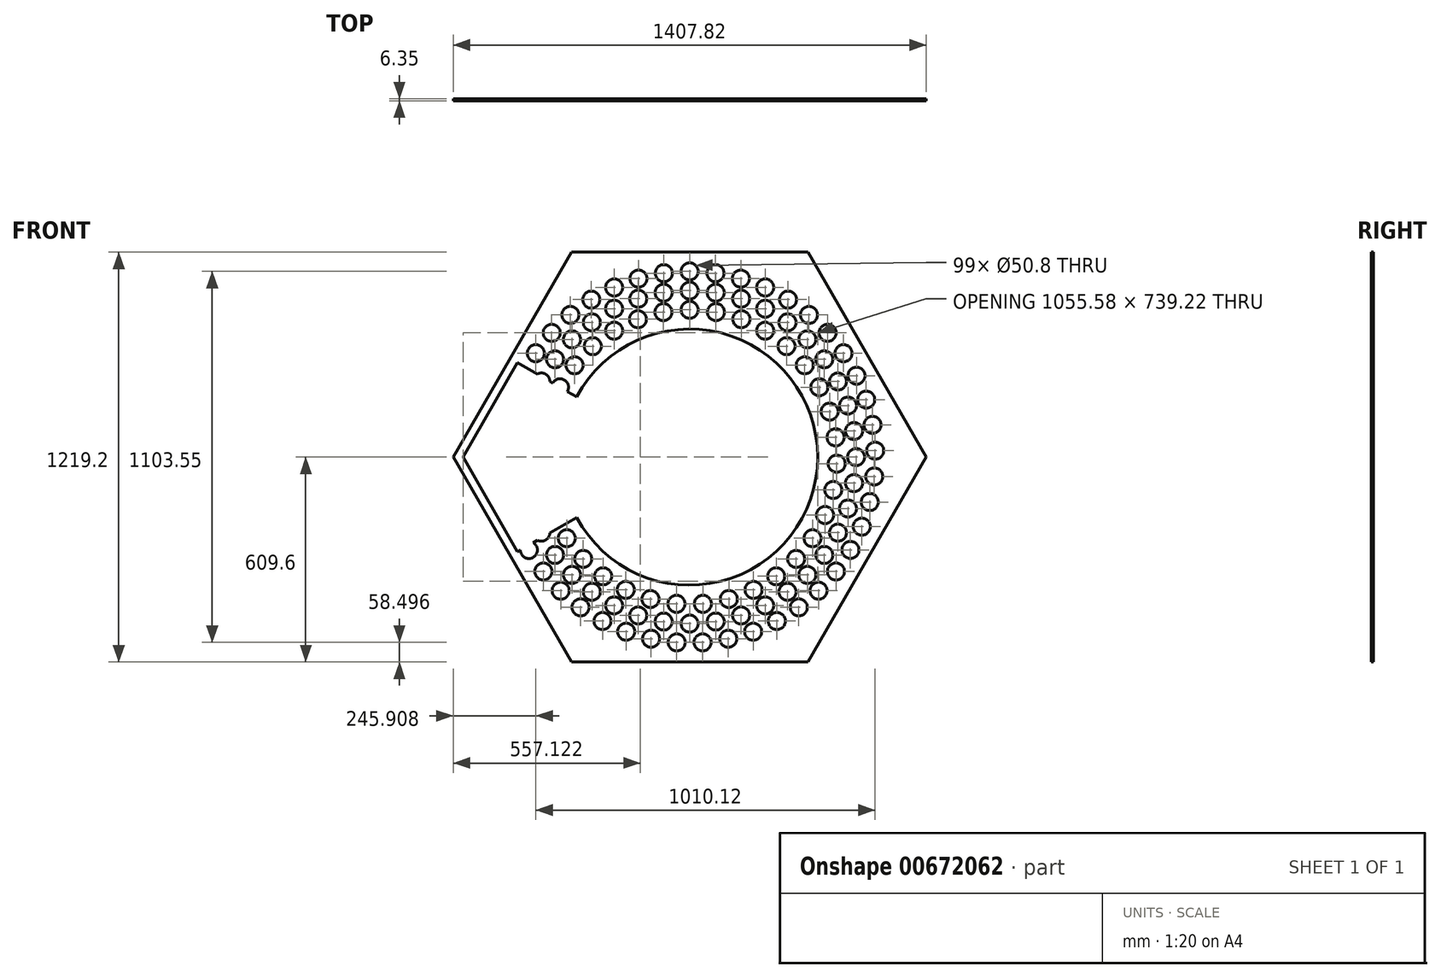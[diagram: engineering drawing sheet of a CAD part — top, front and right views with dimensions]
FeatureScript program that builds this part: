
annotation { "Feature Type Name" : "Feature", "Feature Type Description" : "" }
export const myFeature = defineFeature(function(context is Context, id is Id, definition is map)
    precondition{}
    {
        {
            var Q0;
            Q0=qCreatedBy(makeId("Front.planeOp"),FACE);
            var sketch = newSketch(context, id + "F0", { "sketchPlane" : qUnion([Q0])});
            skCircle(sketch, "E0.cCircle", {"center": v(0, 0) * mm, "radius": 584.2 * mm, "construction": true});
            skLineSegment(sketch, "E0.0", {"start": v(337.29, 584.2) * mm, "end": v(674.58, 0) * mm});
            skLineSegment(sketch, "E0.1", {"start": v(674.58, 0) * mm, "end": v(337.29, -584.2) * mm});
            skLineSegment(sketch, "E0.2", {"start": v(337.29, -584.2) * mm, "end": v(-337.29, -584.2) * mm});
            skLineSegment(sketch, "E0.3", {"start": v(-337.29, -584.2) * mm, "end": v(-674.58, 0) * mm});
            skLineSegment(sketch, "E0.4", {"start": v(-674.58, 0) * mm, "end": v(-499.58, 303.1) * mm});
            skLineSegment(sketch, "E0.5", {"start": v(-337.29, 584.2) * mm, "end": v(337.29, 584.2) * mm});
            skPoint(sketch, "E0.0.midPoint", {"position": v(505.93, 292.1) * mm});
            skCircle(sketch, "E1", {"center": v(0, 0) * mm, "radius": 381 * mm});
            skLineSegment(sketch, "E2", {"start": v(-512.28, 281.1) * mm, "end": v(-336.12, 179.4) * mm});
            skLineSegment(sketch, "E3", {"start": v(-499.58, 303.1) * mm, "end": v(-323.42, 201.4) * mm});
            skLineSegment(sketch, "E4", {"start": v(-337.29, 584.2) * mm, "end": v(-337.29, 584.2) * mm});
            skLineSegment(sketch, "E5", {"start": v(-512.28, 281.1) * mm, "end": v(-337.29, 584.2) * mm});
            skLineSegment(sketch, "E6", {"start": v(-499.58, 303.1) * mm, "end": v(-466.29, 360.76) * mm});
            skLineSegment(sketch, "E7", {"start": v(-674.58, 0) * mm, "end": v(-674.58, 0) * mm});
            skLineSegment(sketch, "E8", {"start": v(-1099.5, 381) * mm, "end": v(1284.02, 381) * mm, "construction": true});
            skLineSegment(sketch, "E9", {"start": v(-1101.82, -381) * mm, "end": v(1466.6, -381) * mm, "construction": true});
            skLineSegment(sketch, "E10.1.0", {"start": v(-499.58, -303.1) * mm, "end": v(-323.42, -201.4) * mm});
            skLineSegment(sketch, "E10.1.1", {"start": v(-512.28, -281.1) * mm, "end": v(-336.12, -179.4) * mm});
            skLineSegment(sketch, "E10.2.0", {"start": v(12.7, -584.2) * mm, "end": v(12.7, -380.79) * mm});
            skLineSegment(sketch, "E10.2.1", {"start": v(-12.7, -584.2) * mm, "end": v(-12.7, -380.79) * mm});
            skLineSegment(sketch, "E10.3.0", {"start": v(512.28, -281.1) * mm, "end": v(336.12, -179.4) * mm});
            skLineSegment(sketch, "E10.3.1", {"start": v(499.58, -303.1) * mm, "end": v(323.42, -201.4) * mm});
            skLineSegment(sketch, "E10.4.0", {"start": v(499.58, 303.1) * mm, "end": v(323.42, 201.4) * mm});
            skLineSegment(sketch, "E10.4.1", {"start": v(512.28, 281.1) * mm, "end": v(336.12, 179.4) * mm});
            skLineSegment(sketch, "E10.5.0", {"start": v(-12.7, 584.2) * mm, "end": v(-12.7, 380.79) * mm});
            skLineSegment(sketch, "E10.5.1", {"start": v(12.7, 584.2) * mm, "end": v(12.7, 380.79) * mm});
            skCircle(sketch, "E11.cCircle", {"center": v(0, 0) * mm, "radius": 609.6 * mm, "construction": true});
            skLineSegment(sketch, "E11.0", {"start": v(-351.95, 609.6) * mm, "end": v(351.95, 609.6) * mm});
            skLineSegment(sketch, "E11.1", {"start": v(351.95, 609.6) * mm, "end": v(703.9, 0) * mm});
            skLineSegment(sketch, "E11.2", {"start": v(703.9, 0) * mm, "end": v(351.95, -609.6) * mm});
            skLineSegment(sketch, "E11.3", {"start": v(351.95, -609.6) * mm, "end": v(-351.95, -609.6) * mm});
            skLineSegment(sketch, "E11.4", {"start": v(-351.95, -609.6) * mm, "end": v(-703.9, 0) * mm});
            skLineSegment(sketch, "E11.5", {"start": v(-703.9, 0) * mm, "end": v(-351.95, 609.6) * mm});
            skPoint(sketch, "E11.0.midPoint", {"position": v(0, 609.6) * mm});
            skSolve(sketch);
        }
        {
            var Q0;
            Q0 = qSketchRegion(id + "F0", true);
            var Q1;
            {var subQ4=sQuery(id+"F0.wireOp",EDGE,"E3");Q1=makeQuery(id+"F0.imprint","IMPRINT",FACE,{"disambiguationData":[TD([[makeQuery(id+"F0.imprint","IMPRINT",EDGE,{"derivedFrom":subQ4}),1.0]])]});}
            var Q2;
            {var subQ0=sQuery(id+"F0.wireOp",EDGE,"E10.5.0");Q2=makeQuery(id+"F0.imprint","IMPRINT",FACE,{"disambiguationData":[TD([[makeQuery(id+"F0.imprint","IMPRINT",EDGE,{"derivedFrom":subQ0}),1.0]])]});}
            var Q3;
            {var subQ0=sQuery(id+"F0.wireOp",EDGE,"E10.4.0");Q3=makeQuery(id+"F0.imprint","IMPRINT",FACE,{"disambiguationData":[TD([[makeQuery(id+"F0.imprint","IMPRINT",EDGE,{"derivedFrom":subQ0}),-1.0]])]});}
            var Q4;
            {var subQ0=sQuery(id+"F0.wireOp",EDGE,"E10.4.0");Q4=makeQuery(id+"F0.imprint","IMPRINT",FACE,{"disambiguationData":[TD([[makeQuery(id+"F0.imprint","IMPRINT",EDGE,{"derivedFrom":subQ0}),1.0]])]});}
            var Q5;
            {var subQ3=sQuery(id+"F0.wireOp",EDGE,"E10.3.0");Q5=makeQuery(id+"F0.imprint","IMPRINT",FACE,{"disambiguationData":[TD([[makeQuery(id+"F0.imprint","IMPRINT",EDGE,{"derivedFrom":subQ3}),-1.0]])]});}
            var Q6;
            {var subQ0=sQuery(id+"F0.wireOp",EDGE,"E10.3.0");Q6=makeQuery(id+"F0.imprint","IMPRINT",FACE,{"disambiguationData":[TD([[makeQuery(id+"F0.imprint","IMPRINT",EDGE,{"derivedFrom":subQ0}),1.0]])]});}
            var Q7;
            {var subQ3=sQuery(id+"F0.wireOp",EDGE,"E10.2.0");Q7=makeQuery(id+"F0.imprint","IMPRINT",FACE,{"disambiguationData":[TD([[makeQuery(id+"F0.imprint","IMPRINT",EDGE,{"derivedFrom":subQ3}),-1.0]])]});}
            var Q8;
            {var subQ0=sQuery(id+"F0.wireOp",EDGE,"E10.2.0");Q8=makeQuery(id+"F0.imprint","IMPRINT",FACE,{"disambiguationData":[TD([[makeQuery(id+"F0.imprint","IMPRINT",EDGE,{"derivedFrom":subQ0}),1.0]])]});}
            var Q9;
            {var subQ3=sQuery(id+"F0.wireOp",EDGE,"E10.1.0");Q9=makeQuery(id+"F0.imprint","IMPRINT",FACE,{"disambiguationData":[TD([[makeQuery(id+"F0.imprint","IMPRINT",EDGE,{"derivedFrom":subQ3}),-1.0]])]});}
            var Q10;
            {var subQ0=sQuery(id+"F0.wireOp",EDGE,"E10.1.0");Q10=makeQuery(id+"F0.imprint","IMPRINT",FACE,{"disambiguationData":[TD([[makeQuery(id+"F0.imprint","IMPRINT",EDGE,{"derivedFrom":subQ0}),1.0]])]});}
            var Q11;
            {var subQ1=sQuery(id+"F0.wireOp",EDGE,"E0.4");Q11=makeQuery(id+"F0.imprint","IMPRINT",FACE,{"disambiguationData":[TD([[makeQuery(id+"F0.imprint","IMPRINT",EDGE,{"derivedFrom":subQ1}),-1.0]])]});}
            var Q12;
            {var subQ0=sQuery(id+"F0.wireOp",EDGE,"E2");Q12=makeQuery(id+"F0.imprint","IMPRINT",FACE,{"disambiguationData":[TD([[makeQuery(id+"F0.imprint","IMPRINT",EDGE,{"derivedFrom":subQ0}),1.0]])]});}
            extrude(context, id + "F1", {"entities" : qUnion([Q0, Q1, Q2, Q3, Q4, Q5, Q6, Q7, Q8, Q9, Q10, Q11, Q12]), "depth" : 6.35 * mm, "offsetDistance" : 25.4 * mm});
        }
        {
            var Q0;
            Q0=qCreatedBy(makeId("Front.planeOp"),FACE);
            var sketch = newSketch(context, id + "F2", { "sketchPlane" : qUnion([Q0])});
            skCircle(sketch, "E12", {"center": v(0, 438.15) * mm, "radius": 25.4 * mm});
            skCircle(sketch, "E13", {"center": v(0, 495.3) * mm, "radius": 25.4 * mm});
            skCircle(sketch, "E14", {"center": v(0, 552.45) * mm, "radius": 25.4 * mm});
            skCircle(sketch, "E15.1.0", {"center": v(-78.23, 431.1) * mm, "radius": 25.4 * mm});
            skCircle(sketch, "E15.2.0", {"center": v(-153.95, 410.21) * mm, "radius": 25.4 * mm});
            skCircle(sketch, "E15.3.0", {"center": v(-224.73, 376.13) * mm, "radius": 25.4 * mm});
            skCircle(sketch, "E15.4.0", {"center": v(-288.28, 329.96) * mm, "radius": 25.4 * mm});
            skCircle(sketch, "E15.5.0", {"center": v(-342.56, 273.18) * mm, "radius": 25.4 * mm});
            skCircle(sketch, "E15.6.0", {"center": v(-385.83, 207.63) * mm, "radius": 25.4 * mm});
            skCircle(sketch, "E15.7.0", {"center": v(-416.7, 135.4) * mm, "radius": 25.4 * mm});
            skCircle(sketch, "E15.8.0", {"center": v(-434.18, 58.81) * mm, "radius": 25.4 * mm});
            skCircle(sketch, "E15.9.0", {"center": v(-437.7, -19.66) * mm, "radius": 25.4 * mm});
            skCircle(sketch, "E15.10.0", {"center": v(-427.16, -97.5) * mm, "radius": 25.4 * mm});
            skCircle(sketch, "E15.11.0", {"center": v(-402.9, -172.2) * mm, "radius": 25.4 * mm});
            skCircle(sketch, "E15.12.0", {"center": v(-365.67, -241.38) * mm, "radius": 25.4 * mm});
            skCircle(sketch, "E15.13.0", {"center": v(-316.7, -302.79) * mm, "radius": 25.4 * mm});
            skCircle(sketch, "E15.14.0", {"center": v(-257.54, -354.47) * mm, "radius": 25.4 * mm});
            skCircle(sketch, "E15.15.0", {"center": v(-190.1, -394.76) * mm, "radius": 25.4 * mm});
            skCircle(sketch, "E15.16.0", {"center": v(-116.56, -422.36) * mm, "radius": 25.4 * mm});
            skCircle(sketch, "E15.17.0", {"center": v(-39.28, -436.39) * mm, "radius": 25.4 * mm});
            skCircle(sketch, "E15.18.0", {"center": v(39.28, -436.39) * mm, "radius": 25.4 * mm});
            skCircle(sketch, "E15.19.0", {"center": v(116.56, -422.36) * mm, "radius": 25.4 * mm});
            skCircle(sketch, "E15.20.0", {"center": v(190.1, -394.76) * mm, "radius": 25.4 * mm});
            skCircle(sketch, "E15.21.0", {"center": v(257.54, -354.47) * mm, "radius": 25.4 * mm});
            skCircle(sketch, "E15.22.0", {"center": v(316.7, -302.79) * mm, "radius": 25.4 * mm});
            skCircle(sketch, "E15.23.0", {"center": v(365.67, -241.38) * mm, "radius": 25.4 * mm});
            skCircle(sketch, "E15.24.0", {"center": v(402.9, -172.2) * mm, "radius": 25.4 * mm});
            skCircle(sketch, "E15.25.0", {"center": v(427.16, -97.5) * mm, "radius": 25.4 * mm});
            skCircle(sketch, "E15.26.0", {"center": v(437.7, -19.66) * mm, "radius": 25.4 * mm});
            skCircle(sketch, "E15.27.0", {"center": v(434.18, 58.81) * mm, "radius": 25.4 * mm});
            skCircle(sketch, "E15.28.0", {"center": v(416.7, 135.4) * mm, "radius": 25.4 * mm});
            skCircle(sketch, "E15.29.0", {"center": v(385.83, 207.63) * mm, "radius": 25.4 * mm});
            skCircle(sketch, "E15.30.0", {"center": v(342.56, 273.18) * mm, "radius": 25.4 * mm});
            skCircle(sketch, "E15.31.0", {"center": v(288.28, 329.96) * mm, "radius": 25.4 * mm});
            skCircle(sketch, "E15.32.0", {"center": v(224.73, 376.13) * mm, "radius": 25.4 * mm});
            skCircle(sketch, "E15.33.0", {"center": v(153.95, 410.21) * mm, "radius": 25.4 * mm});
            skCircle(sketch, "E15.34.0", {"center": v(78.23, 431.1) * mm, "radius": 25.4 * mm});
            skPoint(sketch, "E15.center", {"position": v(0, 0) * mm});
            skCircle(sketch, "E16.1.0", {"center": v(-77.48, 489.2) * mm, "radius": 25.4 * mm});
            skCircle(sketch, "E16.2.0", {"center": v(-153.06, 471.06) * mm, "radius": 25.4 * mm});
            skCircle(sketch, "E16.3.0", {"center": v(-224.86, 441.32) * mm, "radius": 25.4 * mm});
            skCircle(sketch, "E16.4.0", {"center": v(-291.13, 400.7) * mm, "radius": 25.4 * mm});
            skCircle(sketch, "E16.5.0", {"center": v(-350.23, 350.23) * mm, "radius": 25.4 * mm});
            skCircle(sketch, "E16.6.0", {"center": v(-400.7, 291.13) * mm, "radius": 25.4 * mm});
            skCircle(sketch, "E16.7.0", {"center": v(-441.32, 224.86) * mm, "radius": 25.4 * mm});
            skCircle(sketch, "E16.8.0", {"center": v(-471.06, 153.06) * mm, "radius": 25.4 * mm});
            skCircle(sketch, "E16.9.0", {"center": v(-489.2, 77.48) * mm, "radius": 25.4 * mm});
            skCircle(sketch, "E16.10.0", {"center": v(-495.3, 0) * mm, "radius": 25.4 * mm});
            skCircle(sketch, "E16.11.0", {"center": v(-489.2, -77.48) * mm, "radius": 25.4 * mm});
            skCircle(sketch, "E16.12.0", {"center": v(-471.06, -153.06) * mm, "radius": 25.4 * mm});
            skCircle(sketch, "E16.13.0", {"center": v(-441.32, -224.86) * mm, "radius": 25.4 * mm});
            skCircle(sketch, "E16.14.0", {"center": v(-400.7, -291.13) * mm, "radius": 25.4 * mm});
            skCircle(sketch, "E16.15.0", {"center": v(-350.23, -350.23) * mm, "radius": 25.4 * mm});
            skCircle(sketch, "E16.16.0", {"center": v(-291.13, -400.7) * mm, "radius": 25.4 * mm});
            skCircle(sketch, "E16.17.0", {"center": v(-224.86, -441.32) * mm, "radius": 25.4 * mm});
            skCircle(sketch, "E16.18.0", {"center": v(-153.06, -471.06) * mm, "radius": 25.4 * mm});
            skCircle(sketch, "E16.19.0", {"center": v(-77.48, -489.2) * mm, "radius": 25.4 * mm});
            skCircle(sketch, "E16.20.0", {"center": v(0, -495.3) * mm, "radius": 25.4 * mm});
            skCircle(sketch, "E16.21.0", {"center": v(77.48, -489.2) * mm, "radius": 25.4 * mm});
            skCircle(sketch, "E16.22.0", {"center": v(153.06, -471.06) * mm, "radius": 25.4 * mm});
            skCircle(sketch, "E16.23.0", {"center": v(224.86, -441.32) * mm, "radius": 25.4 * mm});
            skCircle(sketch, "E16.24.0", {"center": v(291.13, -400.7) * mm, "radius": 25.4 * mm});
            skCircle(sketch, "E16.25.0", {"center": v(350.23, -350.23) * mm, "radius": 25.4 * mm});
            skCircle(sketch, "E16.26.0", {"center": v(400.7, -291.13) * mm, "radius": 25.4 * mm});
            skCircle(sketch, "E16.27.0", {"center": v(441.32, -224.86) * mm, "radius": 25.4 * mm});
            skCircle(sketch, "E16.28.0", {"center": v(471.06, -153.06) * mm, "radius": 25.4 * mm});
            skCircle(sketch, "E16.29.0", {"center": v(489.2, -77.48) * mm, "radius": 25.4 * mm});
            skCircle(sketch, "E16.30.0", {"center": v(495.3, 0) * mm, "radius": 25.4 * mm});
            skCircle(sketch, "E16.31.0", {"center": v(489.2, 77.48) * mm, "radius": 25.4 * mm});
            skCircle(sketch, "E16.32.0", {"center": v(471.06, 153.06) * mm, "radius": 25.4 * mm});
            skCircle(sketch, "E16.33.0", {"center": v(441.32, 224.86) * mm, "radius": 25.4 * mm});
            skCircle(sketch, "E16.34.0", {"center": v(400.7, 291.13) * mm, "radius": 25.4 * mm});
            skCircle(sketch, "E16.35.0", {"center": v(350.23, 350.23) * mm, "radius": 25.4 * mm});
            skCircle(sketch, "E16.36.0", {"center": v(291.13, 400.7) * mm, "radius": 25.4 * mm});
            skCircle(sketch, "E16.37.0", {"center": v(224.86, 441.32) * mm, "radius": 25.4 * mm});
            skCircle(sketch, "E16.38.0", {"center": v(153.06, 471.06) * mm, "radius": 25.4 * mm});
            skCircle(sketch, "E16.39.0", {"center": v(77.48, 489.2) * mm, "radius": 25.4 * mm});
            skCircle(sketch, "E17.1.0", {"center": v(-76.89, 547.07) * mm, "radius": 25.4 * mm});
            skCircle(sketch, "E17.2.0", {"center": v(-152.28, 531.05) * mm, "radius": 25.4 * mm});
            skCircle(sketch, "E17.3.0", {"center": v(-224.7, 504.69) * mm, "radius": 25.4 * mm});
            skCircle(sketch, "E17.4.0", {"center": v(-292.75, 468.5) * mm, "radius": 25.4 * mm});
            skCircle(sketch, "E17.5.0", {"center": v(-355.1, 423.2) * mm, "radius": 25.4 * mm});
            skCircle(sketch, "E17.6.0", {"center": v(-410.55, 369.66) * mm, "radius": 25.4 * mm});
            skCircle(sketch, "E17.7.0", {"center": v(-458, 308.93) * mm, "radius": 25.4 * mm});
            skCircle(sketch, "E17.8.0", {"center": v(-496.54, 242.18) * mm, "radius": 25.4 * mm});
            skCircle(sketch, "E17.9.0", {"center": v(-525.41, 170.72) * mm, "radius": 25.4 * mm});
            skCircle(sketch, "E17.10.0", {"center": v(-544.06, 95.93) * mm, "radius": 25.4 * mm});
            skCircle(sketch, "E17.11.0", {"center": v(-552.11, 19.28) * mm, "radius": 25.4 * mm});
            skCircle(sketch, "E17.12.0", {"center": v(-549.42, -57.75) * mm, "radius": 25.4 * mm});
            skCircle(sketch, "E17.13.0", {"center": v(-536.04, -133.65) * mm, "radius": 25.4 * mm});
            skCircle(sketch, "E17.14.0", {"center": v(-512.22, -206.95) * mm, "radius": 25.4 * mm});
            skCircle(sketch, "E17.15.0", {"center": v(-478.44, -276.23) * mm, "radius": 25.4 * mm});
            skCircle(sketch, "E17.16.0", {"center": v(-435.34, -340.12) * mm, "radius": 25.4 * mm});
            skCircle(sketch, "E17.17.0", {"center": v(-383.76, -397.4) * mm, "radius": 25.4 * mm});
            skCircle(sketch, "E17.18.0", {"center": v(-324.72, -446.94) * mm, "radius": 25.4 * mm});
            skCircle(sketch, "E17.19.0", {"center": v(-259.36, -487.78) * mm, "radius": 25.4 * mm});
            skCircle(sketch, "E17.20.0", {"center": v(-188.95, -519.13) * mm, "radius": 25.4 * mm});
            skCircle(sketch, "E17.21.0", {"center": v(-114.86, -540.38) * mm, "radius": 25.4 * mm});
            skCircle(sketch, "E17.22.0", {"center": v(-38.54, -551.1) * mm, "radius": 25.4 * mm});
            skCircle(sketch, "E17.23.0", {"center": v(38.54, -551.1) * mm, "radius": 25.4 * mm});
            skCircle(sketch, "E17.24.0", {"center": v(114.86, -540.38) * mm, "radius": 25.4 * mm});
            skCircle(sketch, "E17.25.0", {"center": v(188.95, -519.13) * mm, "radius": 25.4 * mm});
            skCircle(sketch, "E17.26.0", {"center": v(259.36, -487.78) * mm, "radius": 25.4 * mm});
            skCircle(sketch, "E17.27.0", {"center": v(324.72, -446.94) * mm, "radius": 25.4 * mm});
            skCircle(sketch, "E17.28.0", {"center": v(383.76, -397.4) * mm, "radius": 25.4 * mm});
            skCircle(sketch, "E17.29.0", {"center": v(435.34, -340.12) * mm, "radius": 25.4 * mm});
            skCircle(sketch, "E17.30.0", {"center": v(478.44, -276.23) * mm, "radius": 25.4 * mm});
            skCircle(sketch, "E17.31.0", {"center": v(512.22, -206.95) * mm, "radius": 25.4 * mm});
            skCircle(sketch, "E17.32.0", {"center": v(536.04, -133.65) * mm, "radius": 25.4 * mm});
            skCircle(sketch, "E17.33.0", {"center": v(549.42, -57.75) * mm, "radius": 25.4 * mm});
            skCircle(sketch, "E17.34.0", {"center": v(552.11, 19.28) * mm, "radius": 25.4 * mm});
            skCircle(sketch, "E17.35.0", {"center": v(544.06, 95.93) * mm, "radius": 25.4 * mm});
            skCircle(sketch, "E17.36.0", {"center": v(525.41, 170.72) * mm, "radius": 25.4 * mm});
            skCircle(sketch, "E17.37.0", {"center": v(496.54, 242.18) * mm, "radius": 25.4 * mm});
            skCircle(sketch, "E17.38.0", {"center": v(458, 308.93) * mm, "radius": 25.4 * mm});
            skCircle(sketch, "E17.39.0", {"center": v(410.55, 369.66) * mm, "radius": 25.4 * mm});
            skCircle(sketch, "E17.40.0", {"center": v(355.1, 423.2) * mm, "radius": 25.4 * mm});
            skCircle(sketch, "E17.41.0", {"center": v(292.75, 468.5) * mm, "radius": 25.4 * mm});
            skCircle(sketch, "E17.42.0", {"center": v(224.7, 504.69) * mm, "radius": 25.4 * mm});
            skCircle(sketch, "E17.43.0", {"center": v(152.28, 531.05) * mm, "radius": 25.4 * mm});
            skCircle(sketch, "E17.44.0", {"center": v(76.89, 547.07) * mm, "radius": 25.4 * mm});
            skSolve(sketch);
        }
        {
            var Q0;
            Q0 = qSketchRegion(id + "F2", true);
            extrude(context, id + "F3", {"entities" : qUnion([Q0]), "operationType" : NewBodyOperationType.REMOVE, "depth" : 25.4 * mm, "offsetDistance" : 25.4 * mm});
        }
    });
